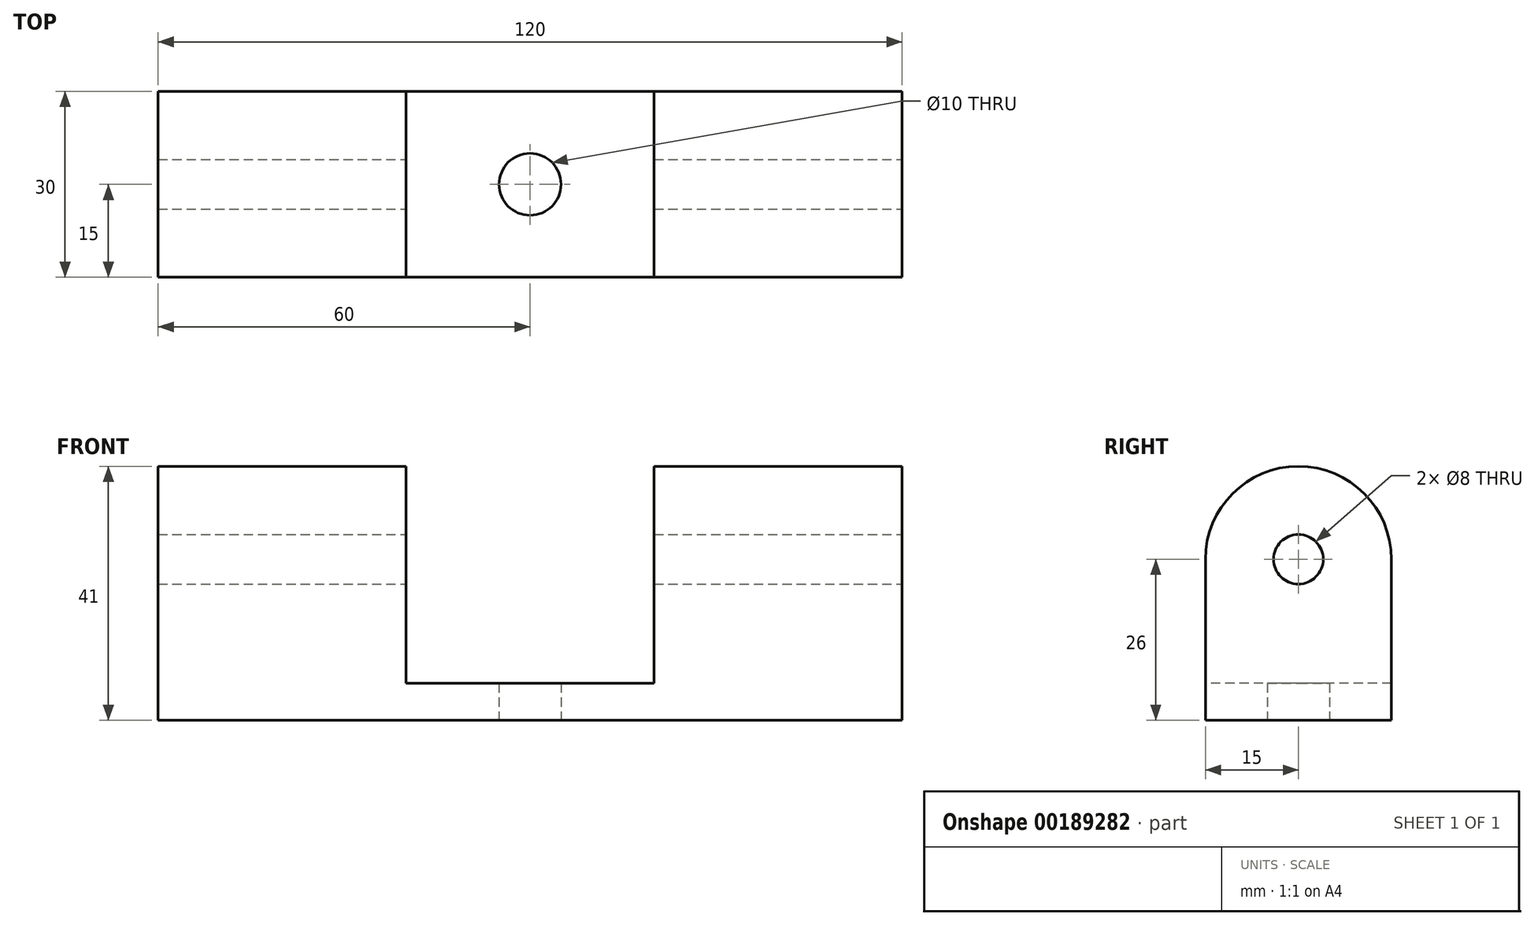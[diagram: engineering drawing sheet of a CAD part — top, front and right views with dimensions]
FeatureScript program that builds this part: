
annotation { "Feature Type Name" : "Feature", "Feature Type Description" : "" }
export const myFeature = defineFeature(function(context is Context, id is Id, definition is map)
    precondition{}
    {
        {
            var Q0;
            Q0=qCreatedBy(makeId("Top.planeOp"),FACE);
            var sketch = newSketch(context, id + "F0", { "sketchPlane" : qUnion([Q0])});
            skLineSegment(sketch, "E0.bottom", {"start": v(60, -15) * mm, "end": v(-60, -15) * mm});
            skLineSegment(sketch, "E0.top", {"start": v(60, 15) * mm, "end": v(-60, 15) * mm});
            skLineSegment(sketch, "E0.left", {"start": v(60, -15) * mm, "end": v(60, 15) * mm});
            skLineSegment(sketch, "E0.right", {"start": v(-60, -15) * mm, "end": v(-60, 15) * mm});
            skPoint(sketch, "E0.middle", {"position": v(0, 0) * mm});
            skCircle(sketch, "E1", {"center": v(0, 0) * mm, "radius": 5 * mm});
            skSolve(sketch);
        }
        {
            var Q0;
            Q0 = qSketchRegion(id + "F0", true);
            extrude(context, id + "F1", {"entities" : qUnion([Q0]), "depth" : 6 * mm});
        }
        {
            var Q0;
            Q0=makeQuery(id+"F1.opExtrude","CAP_FACE",FACE,{"disambiguationData":[OSD([sQuery(id+"F0.wireOp",EDGE,"E0.bottom"),sQuery(id+"F0.wireOp",EDGE,"E0.top"),sQuery(id+"F0.wireOp",EDGE,"E0.left"),sQuery(id+"F0.wireOp",EDGE,"E0.right"),sQuery(id+"F0.wireOp",EDGE,"E1")])],"isStart":false});
            var sketch = newSketch(context, id + "F2", { "sketchPlane" : qUnion([Q0])});
            skLineSegment(sketch, "E2.bottom", {"start": v(-60, 15) * mm, "end": v(-20, 15) * mm});
            skLineSegment(sketch, "E2.top", {"start": v(-60, -15) * mm, "end": v(-20, -15) * mm});
            skLineSegment(sketch, "E2.left", {"start": v(-60, 15) * mm, "end": v(-60, -15) * mm});
            skLineSegment(sketch, "E2.right", {"start": v(-20, 15) * mm, "end": v(-20, -15) * mm});
            skLineSegment(sketch, "E3.bottom", {"start": v(60, 15) * mm, "end": v(20, 15) * mm});
            skLineSegment(sketch, "E3.top", {"start": v(60, -15) * mm, "end": v(20, -15) * mm});
            skLineSegment(sketch, "E3.left", {"start": v(60, 15) * mm, "end": v(60, -15) * mm});
            skLineSegment(sketch, "E3.right", {"start": v(20, 15) * mm, "end": v(20, -15) * mm});
            skSolve(sketch);
        }
        {
            var Q0;
            Q0 = qSketchRegion(id + "F2", true);
            extrude(context, id + "F3", {"entities" : qUnion([Q0]), "operationType" : NewBodyOperationType.ADD, "depth" : 35 * mm});
        }
        {
            var Q0;
            Q0=makeQuery(id+"F3.boolean.opBoolean","MERGE",FACE,{"derivedFrom":[makeQuery(id+"F1.opExtrude","SWEPT_FACE",FACE,{"disambiguationData":[OSD([sQuery(id+"F0.wireOp",EDGE,"E0.left")])]}),makeQuery(id+"F3.opExtrude","SWEPT_FACE",FACE,{"disambiguationData":[OSD([sQuery(id+"F2.wireOp",EDGE,"E3.left")])]})]});
            var sketch = newSketch(context, id + "F4", { "sketchPlane" : qUnion([Q0])});
            skLineSegment(sketch, "E4.0", {"start": v(-15, 41) * mm, "end": v(15, 41) * mm});
            skLineSegment(sketch, "E4.1", {"start": v(-15, 41) * mm, "end": v(-15, 0) * mm});
            skLineSegment(sketch, "E4.2", {"start": v(15, 41) * mm, "end": v(15, 0) * mm});
            skLineSegment(sketch, "E5", {"start": v(0, 41) * mm, "end": v(0, 26) * mm});
            skPoint(sketch, "E5.endSnap0", {"position": v(0, 41) * mm});
            skCircle(sketch, "E6", {"center": v(0, 26) * mm, "radius": 15 * mm});
            skCircle(sketch, "E7", {"center": v(0, 26) * mm, "radius": 4 * mm});
            skSolve(sketch);
        }
        {
            var Q0;
            {var subQ0=sQuery(id+"F4.wireOp",EDGE,"E4.1");var subQ1=sQuery(id+"F4.wireOp",EDGE,"E4.0");var subQ2=makeQuery(id+"F4.imprint","INTERSECT",VERTEX,{"derivedFrom":[subQ1,subQ0]});Q0=makeQuery(id+"F4.imprint","IMPRINT",FACE,{"disambiguationData":[TD([[makeQuery(id+"F4.imprint","IMPRINT",EDGE,{"disambiguationData":[TD([[subQ2,-1.0]])],"derivedFrom":subQ1}),-1.0]])]});}
            var Q1;
            {var subQ0=sQuery(id+"F4.wireOp",EDGE,"E4.2");var subQ1=sQuery(id+"F4.wireOp",EDGE,"E4.0");var subQ2=makeQuery(id+"F4.imprint","INTERSECT",VERTEX,{"derivedFrom":[subQ1,subQ0]});Q1=makeQuery(id+"F4.imprint","IMPRINT",FACE,{"disambiguationData":[TD([[makeQuery(id+"F4.imprint","IMPRINT",EDGE,{"disambiguationData":[TD([[subQ2,1.0]])],"derivedFrom":subQ1}),-1.0]])]});}
            var Q2;
            Q2=makeQuery(id+"F4.imprint","IMPRINT",FACE,{"disambiguationData":[TD([[makeQuery(id+"F4.imprint","IMPRINT",EDGE,{"derivedFrom":sQuery(id+"F4.wireOp",EDGE,"E7")}),1.0]])]});
            extrude(context, id + "F5", {"entities" : qUnion([Q0, Q1, Q2]), "operationType" : NewBodyOperationType.REMOVE, "oppositeDirection" : true, "depth" : 122 * mm});
        }
    });
